# Revit family: No interlocked sockets  20_25 V
name_source: partatom
category: Installations électriques
revit_build: Autodesk Revit 2018 (Build: 20170223_1515(x64)
units: mm (PartAtom-declared; Revit-internal decimal feet)

## family parameters
Conserver l'orientation des annotations = Non
Cote de connecteur circulaire = Utiliser le diamètre
Couper avec des vides une fois chargée = Non
Hôte = Face
Partagée = Non
Point de calcul de pièce = Non
Type d'élément = Normal

## types (2) — shared parameters
Elévation par défaut = 1000 mm  [stored 3.28084 ft]
Fabricant = Legrand
Flush E or Surface mounting S = flush and surface mounting
International standard socket for flush mounting or surface mounting with accessory allows the connection of power devices = International standard socket for flush mounting or surface mounting with accessory allows the connection of power devices
Maximum use temperature = 40
Minimum use temperature = -25
Number of poles = 2
Product family = 0854-P17 TEMPRA PRO
Standard IEC or NFC = IEC
Tension V = 20 25 V  50/60 Hz purple
characteristic color = purple
connecting type = screw terminals
depth for flush mounting mm = 33 mm  [stored 0.108268 ft]
depth mm = 66 mm
halogen free = Oui
height mm = 84 mm
horizontal fixing distance mm = 70 mm
material of box = plastic
protection class IP = IP44
resistance to chocks IK = 9
vertical fixing distance mm = 70 mm
width mm = 84 mm
zero-valued in all types: Position of earth h

## per-type parameters (varying)
| type | Description | intensity A |
| P17 - IP44 - 32A - 2P | LG-055295_Panel mounting socket P17 - IP 44 - 20/25 V - 32 A - 2P | 32 A |
| P17 - IP44 - 16 A - 2P | LG-055245_ P17 - IP 44 - 20/25 V - 16 A - 2P | 16 A |

note: [stored X ft] marks values corroborated as IEEE doubles in the binary element streams (Revit-internal decimal feet)
